# Revit family: Hager-UNIVERS-Surface_mounted-IP44-With_Cover-With_DIN-Hosted-DE-de
name_source: partatom
category: Electrical Equipment
units: mm (PartAtom-declared; Revit-internal decimal feet)

## family parameters
Cut with Voids When Loaded = No
Host = Face
Maintain Annotation Orientation = Yes
Panel Configuration = Two Columns, Circuits Across
Part Type = Panelboard
Room Calculation Point = No
Round Connector Dimension = Use Diameter
Shared = No

## types (114) — shared parameters
BC_MODEL_ID = 1539184
BC_OBJECT_ID = 512283
BC_OBJECT_VERSION = #6
Code hager = ADD-EC000214_EU
EF000007 - Farbe = weiß
EF000024 - UV-beständig = No
EF000049 - Tiefe = 165 mm  [stored 0.541339 ft]
EF000116 - RAL-Nummer = 9010
EF000118 - Mit Montageplatte = No
EF001062 - EMV-Ausführung = No
EF001088 - Anbaumöglichkeit = Yes
EF001134 - DIN-Schiene = Yes
EF004462 - Art der Schließung = sonstige
EF005474 - Schutzart (IP) = IP44
EF006306 - Mit Schloss = No
EF015941 - Signaldurchlassende Tür = No
ETIM class code = EC000214
ETIM class name = Small distribution board
HG000002-Mit tür = Yes
HG000003-Bereich = UNIVERS
HG000005-Dicke = 2 mm  [stored 0.00656168 ft]
HG000006-Flush mounted = No
HG000011-Leere Reihen von unten = No
HG000012-Türschwenkwinkel = 90.00°
HG000013-Tür links = No
HG000014-Tür rechts = Yes
HG000015-Sichtbarkeit der Türöffnung = Yes
HG000016-3D-Türsichtbarkeit = Yes
HG000017-Distanz zwischen den Polen = 18 mm  [stored 0.0590551 ft]
HG000060-RAL-number = 9010
HG000099-Onfly Template ID-de-DE = 507532
Manufacturer = Hager
Name = Hager-UNIVERS-Surface_mounted-IP44-With_Cover-With_DIN-NoHosted-DE-de
Name BIM&CO = Electricity
Name hager = ADD_Enclosures_EC000214
Uniformat = Low Tension Service & Dist.
Uniformat code = D501001
zero-valued in all types: Default Elevation, EF001131 - Innentiefe

## per-type parameters (varying)
| type | BC_VARIANT_ID | EF000003 - Montageart | EF000008 - Breite | EF000040 - Höhe | EF000218 - Einbautiefe | EF000266 - Anzahl der Reihen | EF000332 - Einbauhöhe | EF000846 - Einbaubreite | EF002950 - Breite in Teilungseinheiten | EF006244 - Transparenter Deckel/Tür | EF009212 - Ausführung Deckel | EF015776 - Erdungsklemmenblock | EF015777 - Neutralleiterklemmenblock | HG000001-Anzahl der Spalten | HG000004-Herstellerreferenz | HG000007-Anzahl der leeren Spalten | HG000008-Anzahl der leeren Reihen | HG000009-Doppelflügeligen Tür | HG000010-Asymmetrische Türen | HGEF000266-Anzahl der Reihen | HGEF0002950-Breite in Teilungseinheiten |
| UNIVERS-Surface_mounted_W300_H500_D165_12_Modular_Spacing-FWB31 | 1169536 | Aufputz | 300 mm | 500 mm  [stored 1.64042 ft] | 161 mm  [stored 0.528215 ft] | 3 | 500 mm  [stored 1.64042 ft] | 300 mm | 12 | No | mit Ausschnitt | No | Yes | 1 | FWB31 | 0 | 0 | No | No | 3 | 12 |
| UNIVERS-Surface_mounted_W300_H500_D165_12_Modular_Spacing-FWB31A | 1169538 | Aufputz | 300 mm | 500 mm  [stored 1.64042 ft] | 161 mm  [stored 0.528215 ft] | 3 | 500 mm  [stored 1.64042 ft] | 300 mm | 12 | No | mit Ausschnitt | No | No | 1 | FWB31A | 0 | 0 | No | No | 3 | 12 |
| UNIVERS-Surface_mounted_W300_H500_D165_12_Modular_Spacing-FWB31GS | 1169539 | Aufputz | 300 mm | 500 mm  [stored 1.64042 ft] | 161 mm  [stored 0.528215 ft] | 3 | 500 mm  [stored 1.64042 ft] | 300 mm | 12 | Yes | mit Ausschnitt | Yes | Yes | 1 | FWB31GS | 0 | 0 | No | No | 3 | 12 |
| UNIVERS-Surface_mounted_W300_H500_D165_12_Modular_Spacing-FWB31P | 1169540 | Aufputz | 300 mm | 500 mm  [stored 1.64042 ft] | 161 mm  [stored 0.528215 ft] | 3 | 500 mm  [stored 1.64042 ft] | 300 mm | 12 | No | geschlossen | No | No | 1 | FWB31P | 0 | 0 | No | No | 3 | 12 |
| UNIVERS-Surface_mounted_W300_H500_D165_12_Modular_Spacing-FWB31S | 1169541 | Aufputz | 300 mm | 500 mm  [stored 1.64042 ft] | 161 mm  [stored 0.528215 ft] | 3 | 500 mm  [stored 1.64042 ft] | 300 mm | 12 | No | mit Ausschnitt | Yes | Yes | 1 | FWB31S | 0 | 0 | No | No | 3 | 12 |
| UNIVERS-Surface_mounted_W550_H500_D165_24_Modular_Spacing-FWB32 | 1169543 | Aufputz | 550 mm | 500 mm  [stored 1.64042 ft] | 161 mm  [stored 0.528215 ft] | 3 | 500 mm  [stored 1.64042 ft] | 550 mm | 24 | No | mit Ausschnitt | No | Yes | 2 | FWB32 | 0 | 0 | No | No | 3 | 24 |
| UNIVERS-Surface_mounted_W550_H500_D165_24_Modular_Spacing-FWB32A | 1169545 | Aufputz | 550 mm | 500 mm  [stored 1.64042 ft] | 161 mm  [stored 0.528215 ft] | 3 | 500 mm  [stored 1.64042 ft] | 550 mm | 24 | No | mit Ausschnitt | No | No | 2 | FWB32A | 0 | 0 | No | No | 3 | 24 |
| UNIVERS-Surface_mounted_W550_H500_D165_24_Modular_Spacing-FWB32GS | 1169546 | Aufputz | 550 mm | 500 mm  [stored 1.64042 ft] | 161 mm  [stored 0.528215 ft] | 3 | 500 mm  [stored 1.64042 ft] | 550 mm | 24 | Yes | mit Ausschnitt | Yes | Yes | 2 | FWB32GS | 0 | 0 | No | No | 3 | 24 |
| UNIVERS-Surface_mounted_W550_H500_D165_24_Modular_Spacing-FWB32P | 1169547 | Aufputz | 550 mm | 500 mm  [stored 1.64042 ft] | 161 mm  [stored 0.528215 ft] | 3 | 500 mm  [stored 1.64042 ft] | 550 mm | 24 | No | geschlossen | No | No | 2 | FWB32P | 0 | 0 | No | No | 3 | 24 |
| UNIVERS-Surface_mounted_W550_H500_D165_24_Modular_Spacing-FWB32S | 1169549 | Aufputz | 550 mm | 500 mm  [stored 1.64042 ft] | 161 mm  [stored 0.528215 ft] | 3 | 500 mm  [stored 1.64042 ft] | 550 mm | 24 | No | mit Ausschnitt | Yes | Yes | 2 | FWB32S | 0 | 0 | No | No | 3 | 24 |
| UNIVERS-Surface_mounted_W800_H500_D165_36_Modular_Spacing-FWB33 | 1169551 | Aufputz | 800 mm  [stored 2.62467 ft] | 500 mm  [stored 1.64042 ft] | 161 mm  [stored 0.528215 ft] | 3 | 500 mm  [stored 1.64042 ft] | 800 mm  [stored 2.62467 ft] | 36 | No | mit Ausschnitt | No | Yes | 3 | FWB33 | 0 | 0 | Yes | Yes | 3 | 36 |
| UNIVERS-Surface_mounted_W800_H500_D165_36_Modular_Spacing-FWB33A | 1169553 | Aufputz | 800 mm  [stored 2.62467 ft] | 500 mm  [stored 1.64042 ft] | 161 mm  [stored 0.528215 ft] | 3 | 500 mm  [stored 1.64042 ft] | 800 mm  [stored 2.62467 ft] | 36 | No | mit Ausschnitt | No | No | 3 | FWB33A | 0 | 0 | Yes | Yes | 3 | 36 |
| UNIVERS-Surface_mounted_W800_H500_D165_36_Modular_Spacing-FWB33GS | 1169554 | Aufputz | 800 mm  [stored 2.62467 ft] | 500 mm  [stored 1.64042 ft] | 161 mm  [stored 0.528215 ft] | 3 | 500 mm  [stored 1.64042 ft] | 800 mm  [stored 2.62467 ft] | 36 | Yes | mit Ausschnitt | Yes | Yes | 3 | FWB33GS | 0 | 0 | Yes | Yes | 3 | 36 |
| UNIVERS-Surface_mounted_W800_H500_D165_36_Modular_Spacing-FWB33P | 1169556 | Aufputz | 800 mm  [stored 2.62467 ft] | 500 mm  [stored 1.64042 ft] | 161 mm  [stored 0.528215 ft] | 3 | 500 mm  [stored 1.64042 ft] | 800 mm  [stored 2.62467 ft] | 36 | No | mit Ausschnitt | No | No | 3 | FWB33P | 0 | 0 | Yes | Yes | 3 | 36 |
| UNIVERS-Surface_mounted_W800_H500_D165_36_Modular_Spacing-FWB33S | 1169558 | Aufputz | 800 mm  [stored 2.62467 ft] | 500 mm  [stored 1.64042 ft] | 161 mm  [stored 0.528215 ft] | 3 | 500 mm  [stored 1.64042 ft] | 800 mm  [stored 2.62467 ft] | 36 | No | mit Ausschnitt | Yes | Yes | 3 | FWB33S | 0 | 0 | Yes | Yes | 3 | 36 |
| UNIVERS-Surface_mounted_W1050_H500_D165_48_Modular_Spacing-FWB34 | 1169560 | Aufputz | 1050 mm | 500 mm  [stored 1.64042 ft] | 161 mm  [stored 0.528215 ft] | 3 | 500 mm  [stored 1.64042 ft] | 1050 mm | 48 | No | mit Ausschnitt | No | Yes | 4 | FWB34 | 0 | 0 | Yes | No | 3 | 48 |
| UNIVERS-Surface_mounted_W1050_H500_D165_48_Modular_Spacing-FWB34A | 1169562 | Aufputz | 1050 mm | 500 mm  [stored 1.64042 ft] | 161 mm  [stored 0.528215 ft] | 3 | 500 mm  [stored 1.64042 ft] | 1050 mm | 48 | No | mit Ausschnitt | No | No | 4 | FWB34A | 0 | 0 | Yes | No | 3 | 48 |
| UNIVERS-Surface_mounted_W1050_H500_D165_48_Modular_Spacing-FWB34GS | 1169564 | Aufputz | 1050 mm | 500 mm  [stored 1.64042 ft] | 161 mm  [stored 0.528215 ft] | 3 | 500 mm  [stored 1.64042 ft] | 1050 mm | 48 | Yes | mit Ausschnitt | Yes | Yes | 4 | FWB34GS | 0 | 0 | Yes | No | 3 | 48 |
| UNIVERS-Surface_mounted_W1050_H500_D165_48_Modular_Spacing-FWB34P | 1169567 | Aufputz | 1050 mm | 500 mm  [stored 1.64042 ft] | 161 mm  [stored 0.528215 ft] | 3 | 500 mm  [stored 1.64042 ft] | 1050 mm | 48 | No | geschlossen | No | No | 4 | FWB34P | 0 | 0 | Yes | No | 3 | 48 |
| UNIVERS-Surface_mounted_W1050_H500_D165_48_Modular_Spacing-FWB34S | 1169569 | Aufputz | 1050 mm | 500 mm  [stored 1.64042 ft] | 161 mm  [stored 0.528215 ft] | 3 | 500 mm  [stored 1.64042 ft] | 1050 mm | 48 | No | mit Ausschnitt | Yes | Yes | 4 | FWB34S | 0 | 0 | Yes | No | 3 | 48 |
| UNIVERS-Surface_mounted_W300_H650_D165_12_Modular_Spacing-FWB41 | 1169571 | Aufputz | 300 mm | 650 mm  [stored 2.13255 ft] | 161 mm  [stored 0.528215 ft] | 4 | 650 mm  [stored 2.13255 ft] | 300 mm | 12 | No | mit Ausschnitt | No | Yes | 1 | FWB41 | 0 | 0 | No | No | 4 | 12 |
| UNIVERS-Surface_mounted_W300_H650_D165_12_Modular_Spacing-FWB41A | 1169573 | Aufputz | 300 mm | 650 mm  [stored 2.13255 ft] | 161 mm  [stored 0.528215 ft] | 4 | 650 mm  [stored 2.13255 ft] | 300 mm | 12 | No | mit Ausschnitt | No | No | 1 | FWB41A | 0 | 0 | No | No | 4 | 12 |
| UNIVERS-Surface_mounted_W300_H650_D165_12_Modular_Spacing-FWB41GS | 1169574 | Aufputz | 300 mm | 650 mm  [stored 2.13255 ft] | 161 mm  [stored 0.528215 ft] | 4 | 650 mm  [stored 2.13255 ft] | 300 mm | 12 | Yes | mit Ausschnitt | Yes | Yes | 1 | FWB41GS | 0 | 0 | No | No | 4 | 12 |
| UNIVERS-Surface_mounted_W300_H650_D165_12_Modular_Spacing-FWB41P | 1169577 | Aufputz | 300 mm | 650 mm  [stored 2.13255 ft] | 161 mm  [stored 0.528215 ft] | 4 | 650 mm  [stored 2.13255 ft] | 300 mm | 12 | No | geschlossen | No | No | 1 | FWB41P | 0 | 0 | No | No | 4 | 12 |
| UNIVERS-Surface_mounted_W300_H650_D165_12_Modular_Spacing-FWB41S | 1169579 | Aufputz | 300 mm | 650 mm  [stored 2.13255 ft] | 161 mm  [stored 0.528215 ft] | 4 | 650 mm  [stored 2.13255 ft] | 300 mm | 12 | No | mit Ausschnitt | Yes | Yes | 1 | FWB41S | 0 | 0 | No | No | 4 | 12 |
| UNIVERS-Surface_mounted_W550_H650_D165_24_Modular_Spacing-FWB42 | 1169580 | Aufputz | 550 mm | 650 mm  [stored 2.13255 ft] | 161 mm  [stored 0.528215 ft] | 4 | 650 mm  [stored 2.13255 ft] | 550 mm | 24 | No | mit Ausschnitt | No | Yes | 2 | FWB42 | 0 | 0 | No | No | 4 | 24 |
| UNIVERS-Surface_mounted_W550_H650_D165_24_Modular_Spacing-FWB42A | 1169582 | Aufputz | 550 mm | 650 mm  [stored 2.13255 ft] | 161 mm  [stored 0.528215 ft] | 4 | 650 mm  [stored 2.13255 ft] | 550 mm | 24 | No | mit Ausschnitt | No | No | 2 | FWB42A | 0 | 0 | No | No | 4 | 24 |
| UNIVERS-Surface_mounted_W550_H650_D165_24_Modular_Spacing-FWB42GS | 1169584 | Aufputz | 550 mm | 650 mm  [stored 2.13255 ft] | 161 mm  [stored 0.528215 ft] | 4 | 650 mm  [stored 2.13255 ft] | 550 mm | 24 | Yes | mit Ausschnitt | Yes | Yes | 2 | FWB42GS | 0 | 0 | No | No | 4 | 24 |
| UNIVERS-Surface_mounted_W550_H650_D165_24_Modular_Spacing-FWB42P | 1169587 | Aufputz | 550 mm | 650 mm  [stored 2.13255 ft] | 161 mm  [stored 0.528215 ft] | 4 | 650 mm  [stored 2.13255 ft] | 550 mm | 24 | No | geschlossen | No | No | 2 | FWB42P | 0 | 0 | No | No | 4 | 24 |
| UNIVERS-Surface_mounted_W550_H650_D165_24_Modular_Spacing-FWB42P2 | 1169589 | Aufputz/Unterputz | 550 mm | 650 mm  [stored 2.13255 ft] | 161 mm  [stored 0.528215 ft] | 4 | 650 mm  [stored 2.13255 ft] | 550 mm | 24 | No | mit Ausschnitt | Yes | No | 1 | FWB42P2 | 1 | 0 | No | No | 4 | 24 |
| UNIVERS-Surface_mounted_W550_H650_D165_24_Modular_Spacing-FWB42S | 1169590 | Aufputz/Unterputz | 550 mm | 650 mm  [stored 2.13255 ft] | 161 mm  [stored 0.528215 ft] | 4 | 650 mm  [stored 2.13255 ft] | 550 mm | 24 | No | mit Ausschnitt | Yes | Yes | 2 | FWB42S | 0 | 0 | No | No | 4 | 24 |
| UNIVERS-Surface_mounted_W800_H650_D165_36_Modular_Spacing-FWB43 | 1169592 | Aufputz | 800 mm  [stored 2.62467 ft] | 650 mm  [stored 2.13255 ft] | 161 mm  [stored 0.528215 ft] | 4 | 650 mm  [stored 2.13255 ft] | 800 mm  [stored 2.62467 ft] | 36 | No | mit Ausschnitt | No | Yes | 3 | FWB43 | 0 | 0 | Yes | Yes | 4 | 36 |
| UNIVERS-Surface_mounted_W800_H650_D165_36_Modular_Spacing-FWB43A | 1169593 | Aufputz | 800 mm  [stored 2.62467 ft] | 650 mm  [stored 2.13255 ft] | 161 mm  [stored 0.528215 ft] | 4 | 650 mm  [stored 2.13255 ft] | 800 mm  [stored 2.62467 ft] | 36 | No | mit Ausschnitt | No | No | 3 | FWB43A | 0 | 0 | Yes | Yes | 4 | 36 |
| UNIVERS-Surface_mounted_W800_H650_D165_36_Modular_Spacing-FWB43GS | 1169596 | Aufputz | 800 mm  [stored 2.62467 ft] | 650 mm  [stored 2.13255 ft] | 161 mm  [stored 0.528215 ft] | 4 | 650 mm  [stored 2.13255 ft] | 800 mm  [stored 2.62467 ft] | 36 | Yes | mit Ausschnitt | Yes | Yes | 3 | FWB43GS | 0 | 0 | Yes | Yes | 4 | 36 |
| UNIVERS-Surface_mounted_W800_H650_D165_36_Modular_Spacing-FWB43P | 1169597 | Aufputz | 800 mm  [stored 2.62467 ft] | 650 mm  [stored 2.13255 ft] | 161 mm  [stored 0.528215 ft] | 4 | 650 mm  [stored 2.13255 ft] | 800 mm  [stored 2.62467 ft] | 36 | No | geschlossen | No | No | 3 | FWB43P | 0 | 0 | Yes | Yes | 4 | 36 |
| UNIVERS-Surface_mounted_W800_H650_D165_36_Modular_Spacing-FWB43S | 1169598 | Aufputz | 800 mm  [stored 2.62467 ft] | 650 mm  [stored 2.13255 ft] | 161 mm  [stored 0.528215 ft] | 4 | 650 mm  [stored 2.13255 ft] | 800 mm  [stored 2.62467 ft] | 36 | No | mit Ausschnitt | Yes | Yes | 3 | FWB43S | 0 | 0 | Yes | Yes | 4 | 36 |
| UNIVERS-Surface_mounted_W1050_H650_D165_48_Modular_Spacing-FWB44 | 1169599 | Aufputz | 1050 mm | 650 mm  [stored 2.13255 ft] | 161 mm  [stored 0.528215 ft] | 4 | 650 mm  [stored 2.13255 ft] | 1050 mm | 48 | No | mit Ausschnitt | No | Yes | 4 | FWB44 | 0 | 0 | Yes | No | 4 | 48 |
| UNIVERS-Surface_mounted_W1050_H650_D165_48_Modular_Spacing-FWB44A | 1169600 | Aufputz | 1050 mm | 650 mm  [stored 2.13255 ft] | 161 mm  [stored 0.528215 ft] | 4 | 650 mm  [stored 2.13255 ft] | 1050 mm | 48 | No | mit Ausschnitt | No | No | 4 | FWB44A | 0 | 0 | Yes | No | 4 | 48 |
| UNIVERS-Surface_mounted_W1050_H650_D165_48_Modular_Spacing-FWB44GS | 1169602 | Aufputz | 1050 mm | 650 mm  [stored 2.13255 ft] | 161 mm  [stored 0.528215 ft] | 4 | 650 mm  [stored 2.13255 ft] | 1050 mm | 48 | Yes | mit Ausschnitt | Yes | Yes | 4 | FWB44GS | 0 | 0 | Yes | No | 4 | 48 |
| UNIVERS-Surface_mounted_W1050_H650_D165_48_Modular_Spacing-FWB44P | 1169603 | Aufputz | 1050 mm | 650 mm  [stored 2.13255 ft] | 161 mm  [stored 0.528215 ft] | 4 | 650 mm  [stored 2.13255 ft] | 1050 mm | 48 | No | geschlossen | No | No | 4 | FWB44P | 0 | 0 | Yes | No | 4 | 48 |
| UNIVERS-Surface_mounted_W1050_H650_D165_48_Modular_Spacing-FWB44S | 1169604 | Aufputz | 1050 mm | 650 mm  [stored 2.13255 ft] | 161 mm  [stored 0.528215 ft] | 4 | 650 mm  [stored 2.13255 ft] | 1050 mm | 48 | No | mit Ausschnitt | Yes | Yes | 4 | FWB44S | 0 | 0 | Yes | No | 4 | 48 |
| UNIVERS-Surface_mounted_W300_H800_D165_12_Modular_Spacing-FWB51 | 1169606 | Aufputz | 300 mm | 800 mm  [stored 2.62467 ft] | 161 mm  [stored 0.528215 ft] | 5 | 800 mm  [stored 2.62467 ft] | 300 mm | 12 | No | mit Ausschnitt | No | Yes | 1 | FWB51 | 0 | 0 | No | No | 5 | 12 |
| UNIVERS-Surface_mounted_W300_H800_D165_12_Modular_Spacing-FWB51A | 1169608 | Aufputz | 300 mm | 800 mm  [stored 2.62467 ft] | 161 mm  [stored 0.528215 ft] | 5 | 800 mm  [stored 2.62467 ft] | 300 mm | 12 | No | mit Ausschnitt | No | No | 1 | FWB51A | 0 | 0 | No | No | 5 | 12 |
| UNIVERS-Surface_mounted_W300_H800_D165_12_Modular_Spacing-FWB51GS | 1169609 | Aufputz | 300 mm | 800 mm  [stored 2.62467 ft] | 161 mm  [stored 0.528215 ft] | 5 | 800 mm  [stored 2.62467 ft] | 300 mm | 12 | Yes | mit Ausschnitt | Yes | Yes | 1 | FWB51GS | 0 | 0 | No | No | 5 | 12 |
| UNIVERS-Surface_mounted_W300_H800_D165_12_Modular_Spacing-FWB51P | 1169610 | Aufputz | 300 mm | 800 mm  [stored 2.62467 ft] | 161 mm  [stored 0.528215 ft] | 5 | 800 mm  [stored 2.62467 ft] | 300 mm | 12 | No | geschlossen | No | No | 1 | FWB51P | 0 | 0 | No | No | 5 | 12 |
| UNIVERS-Surface_mounted_W300_H800_D165_12_Modular_Spacing-FWB51S | 1169612 | Aufputz | 300 mm | 800 mm  [stored 2.62467 ft] | 161 mm  [stored 0.528215 ft] | 5 | 800 mm  [stored 2.62467 ft] | 300 mm | 12 | No | mit Ausschnitt | Yes | Yes | 1 | FWB51S | 0 | 0 | No | No | 5 | 12 |
| UNIVERS-Surface_mounted_W550_H800_D165_24_Modular_Spacing-FWB52 | 1169613 | Aufputz | 550 mm | 800 mm  [stored 2.62467 ft] | 161 mm  [stored 0.528215 ft] | 5 | 800 mm  [stored 2.62467 ft] | 550 mm | 24 | No | mit Ausschnitt | No | Yes | 2 | FWB52 | 0 | 0 | No | No | 5 | 24 |
| UNIVERS-Surface_mounted_W550_H800_D165_24_Modular_Spacing-FWB52A | 1169614 | Aufputz | 550 mm | 800 mm  [stored 2.62467 ft] | 161 mm  [stored 0.528215 ft] | 5 | 800 mm  [stored 2.62467 ft] | 550 mm | 24 | No | mit Ausschnitt | No | No | 2 | FWB52A | 0 | 0 | No | No | 5 | 24 |
| UNIVERS-Surface_mounted_W550_H800_D165_24_Modular_Spacing-FWB52GS | 1169616 | Aufputz | 550 mm | 800 mm  [stored 2.62467 ft] | 161 mm  [stored 0.528215 ft] | 5 | 800 mm  [stored 2.62467 ft] | 550 mm | 24 | Yes | mit Ausschnitt | Yes | Yes | 2 | FWB52GS | 0 | 0 | No | No | 5 | 24 |
| UNIVERS-Surface_mounted_W550_H800_D165_24_Modular_Spacing-FWB52N | 1169617 | Aufputz | 550 mm | 800 mm  [stored 2.62467 ft] | 161 mm  [stored 0.528215 ft] | 5 | 800 mm  [stored 2.62467 ft] | 550 mm | 24 | No | mit Ausschnitt | No | No | 2 | FWB52N | 0 | 2 | No | No | 5 | 24 |
| UNIVERS-Surface_mounted_W550_H800_D165_24_Modular_Spacing-FWB52N3 | 1169618 | Aufputz | 550 mm | 800 mm  [stored 2.62467 ft] | 160 mm  [stored 0.524934 ft] | 5 | 800 mm  [stored 2.62467 ft] | 550 mm | 24 | No | mit Ausschnitt | No | No | 2 | FWB52N3 | 0 | 2 | No | No | 5 | 24 |
| UNIVERS-Surface_mounted_W550_H800_D165_24_Modular_Spacing-FWB52P | 1169619 | Aufputz | 550 mm | 800 mm  [stored 2.62467 ft] | 161 mm  [stored 0.528215 ft] | 5 | 800 mm  [stored 2.62467 ft] | 550 mm | 24 | No | geschlossen | No | No | 2 | FWB52P | 0 | 0 | No | No | 5 | 24 |
| UNIVERS-Surface_mounted_W550_H800_D165_24_Modular_Spacing-FWB52P2 | 1169621 | Aufputz/Unterputz | 550 mm | 800 mm  [stored 2.62467 ft] | 161 mm  [stored 0.528215 ft] | 5 | 800 mm  [stored 2.62467 ft] | 550 mm | 24 | No | mit Ausschnitt | Yes | No | 1 | FWB52P2 | 1 | 0 | No | No | 5 | 24 |
| UNIVERS-Surface_mounted_W550_H800_D165_24_Modular_Spacing-FWB52S | 1169622 | Aufputz | 550 mm | 800 mm  [stored 2.62467 ft] | 161 mm  [stored 0.528215 ft] | 5 | 800 mm  [stored 2.62467 ft] | 550 mm | 24 | No | mit Ausschnitt | Yes | Yes | 2 | FWB52S | 0 | 0 | No | No | 5 | 24 |
| UNIVERS-Surface_mounted_W800_H800_D165_36_Modular_Spacing-FWB53 | 1169624 | Aufputz | 800 mm  [stored 2.62467 ft] | 800 mm  [stored 2.62467 ft] | 161 mm  [stored 0.528215 ft] | 5 | 800 mm  [stored 2.62467 ft] | 800 mm  [stored 2.62467 ft] | 36 | No | mit Ausschnitt | No | Yes | 3 | FWB53 | 0 | 0 | Yes | Yes | 5 | 36 |
| UNIVERS-Surface_mounted_W800_H800_D165_36_Modular_Spacing-FWB53A | 1169625 | Aufputz | 800 mm  [stored 2.62467 ft] | 800 mm  [stored 2.62467 ft] | 161 mm  [stored 0.528215 ft] | 5 | 800 mm  [stored 2.62467 ft] | 800 mm  [stored 2.62467 ft] | 36 | No | mit Ausschnitt | No | No | 3 | FWB53A | 0 | 0 | Yes | Yes | 5 | 36 |
| UNIVERS-Surface_mounted_W800_H800_D165_36_Modular_Spacing-FWB53GS | 1169627 | Aufputz | 800 mm  [stored 2.62467 ft] | 800 mm  [stored 2.62467 ft] | 161 mm  [stored 0.528215 ft] | 5 | 800 mm  [stored 2.62467 ft] | 800 mm  [stored 2.62467 ft] | 36 | Yes | mit Ausschnitt | Yes | Yes | 3 | FWB53GS | 0 | 0 | Yes | Yes | 5 | 36 |
| UNIVERS-Surface_mounted_W800_H800_D165_36_Modular_Spacing-FWB53N | 1169628 | Aufputz | 800 mm  [stored 2.62467 ft] | 800 mm  [stored 2.62467 ft] | 161 mm  [stored 0.528215 ft] | 5 | 800 mm  [stored 2.62467 ft] | 800 mm  [stored 2.62467 ft] | 36 | No | mit Ausschnitt | No | No | 3 | FWB53N | 0 | 2 | Yes | Yes | 5 | 36 |
| UNIVERS-Surface_mounted_W800_H800_D165_36_Modular_Spacing-FWB53N3 | 1169629 | Aufputz | 800 mm  [stored 2.62467 ft] | 800 mm  [stored 2.62467 ft] | 161 mm  [stored 0.528215 ft] | 5 | 800 mm  [stored 2.62467 ft] | 800 mm  [stored 2.62467 ft] | 36 | No | mit Ausschnitt | No | No | 3 | FWB53N3 | 0 | 2 | Yes | Yes | 5 | 36 |
| UNIVERS-Surface_mounted_W800_H800_D165_36_Modular_Spacing-FWB53P | 1169631 | Aufputz | 800 mm  [stored 2.62467 ft] | 800 mm  [stored 2.62467 ft] | 161 mm  [stored 0.528215 ft] | 5 | 800 mm  [stored 2.62467 ft] | 800 mm  [stored 2.62467 ft] | 36 | No | geschlossen | No | No | 3 | FWB53P | 0 | 0 | Yes | No | 5 | 36 |
| UNIVERS-Surface_mounted_W800_H800_D165_36_Modular_Spacing-FWB53S | 1169633 | Aufputz | 800 mm  [stored 2.62467 ft] | 800 mm  [stored 2.62467 ft] | 161 mm  [stored 0.528215 ft] | 5 | 800 mm  [stored 2.62467 ft] | 800 mm  [stored 2.62467 ft] | 36 | No | mit Ausschnitt | Yes | Yes | 3 | FWB53S | 0 | 0 | Yes | Yes | 5 | 36 |
| UNIVERS-Surface_mounted_W1050_H800_D165_48_Modular_Spacing-FWB54 | 1169634 | Aufputz | 1050 mm | 800 mm  [stored 2.62467 ft] | 161 mm  [stored 0.528215 ft] | 5 | 800 mm  [stored 2.62467 ft] | 1050 mm | 48 | No | mit Ausschnitt | No | Yes | 4 | FWB54 | 0 | 0 | Yes | No | 5 | 48 |
| UNIVERS-Surface_mounted_W1050_H800_D165_48_Modular_Spacing-FWB54A | 1169635 | Aufputz | 1050 mm | 800 mm  [stored 2.62467 ft] | 161 mm  [stored 0.528215 ft] | 5 | 800 mm  [stored 2.62467 ft] | 1050 mm | 48 | No | mit Ausschnitt | No | No | 4 | FWB54A | 0 | 0 | Yes | No | 5 | 48 |
| UNIVERS-Surface_mounted_W1050_H800_D165_48_Modular_Spacing-FWB54GS | 1169636 | Aufputz | 1050 mm | 800 mm  [stored 2.62467 ft] | 161 mm  [stored 0.528215 ft] | 5 | 800 mm  [stored 2.62467 ft] | 1050 mm | 48 | Yes | mit Ausschnitt | Yes | Yes | 4 | FWB54GS | 0 | 0 | Yes | No | 5 | 48 |
| UNIVERS-Surface_mounted_W1050_H800_D165_48_Modular_Spacing-FWB54P | 1169638 | Aufputz | 1050 mm | 800 mm  [stored 2.62467 ft] | 161 mm  [stored 0.528215 ft] | 5 | 800 mm  [stored 2.62467 ft] | 1050 mm | 48 | No | geschlossen | No | No | 4 | FWB54P | 0 | 0 | Yes | No | 5 | 48 |
| UNIVERS-Surface_mounted_W1050_H800_D165_48_Modular_Spacing-FWB54S | 1169640 | Aufputz | 1050 mm | 800 mm  [stored 2.62467 ft] | 161 mm  [stored 0.528215 ft] | 5 | 800 mm  [stored 2.62467 ft] | 1050 mm | 48 | No | mit Ausschnitt | Yes | Yes | 4 | FWB54S | 0 | 0 | Yes | No | 5 | 48 |
| UNIVERS-Surface_mounted_W300_H950_D165_12_Modular_Spacing-FWB61 | 1169641 | Aufputz | 300 mm | 950 mm  [stored 3.1168 ft] | 161 mm  [stored 0.528215 ft] | 6 | 950 mm  [stored 3.1168 ft] | 300 mm | 12 | No | mit Ausschnitt | No | Yes | 1 | FWB61 | 0 | 0 | No | No | 6 | 12 |
| UNIVERS-Surface_mounted_W300_H950_D165_12_Modular_Spacing-FWB61A | 1169642 | Aufputz | 300 mm | 950 mm  [stored 3.1168 ft] | 161 mm  [stored 0.528215 ft] | 6 | 950 mm  [stored 3.1168 ft] | 300 mm | 12 | No | mit Ausschnitt | No | No | 1 | FWB61A | 0 | 0 | No | No | 6 | 12 |
| UNIVERS-Surface_mounted_W300_H950_D165_12_Modular_Spacing-FWB61GS | 1169644 | Aufputz | 300 mm | 950 mm  [stored 3.1168 ft] | 161 mm  [stored 0.528215 ft] | 6 | 950 mm  [stored 3.1168 ft] | 300 mm | 12 | Yes | mit Ausschnitt | Yes | Yes | 1 | FWB61GS | 0 | 0 | No | No | 6 | 12 |
| UNIVERS-Surface_mounted_W300_H950_D165_12_Modular_Spacing-FWB61P | 1169646 | Aufputz | 300 mm | 950 mm  [stored 3.1168 ft] | 161 mm  [stored 0.528215 ft] | 6 | 950 mm  [stored 3.1168 ft] | 300 mm | 12 | No | geschlossen | No | No | 1 | FWB61P | 0 | 0 | No | No | 6 | 12 |
| UNIVERS-Surface_mounted_W300_H950_D165_12_Modular_Spacing-FWB61S | 1169647 | Aufputz | 300 mm | 950 mm  [stored 3.1168 ft] | 161 mm  [stored 0.528215 ft] | 6 | 950 mm  [stored 3.1168 ft] | 300 mm | 12 | No | mit Ausschnitt | Yes | Yes | 1 | FWB61S | 0 | 0 | No | No | 6 | 12 |
| UNIVERS-Surface_mounted_W550_H950_D165_24_Modular_Spacing-FWB62 | 1169648 | Aufputz | 550 mm | 950 mm  [stored 3.1168 ft] | 161 mm  [stored 0.528215 ft] | 6 | 950 mm  [stored 3.1168 ft] | 550 mm | 24 | No | mit Ausschnitt | No | Yes | 2 | FWB62 | 0 | 0 | No | No | 6 | 24 |
| UNIVERS-Surface_mounted_W550_H950_D165_24_Modular_Spacing-FWB62A | 1169649 | Aufputz | 550 mm | 950 mm  [stored 3.1168 ft] | 161 mm  [stored 0.528215 ft] | 6 | 950 mm  [stored 3.1168 ft] | 550 mm | 24 | No | mit Ausschnitt | No | No | 2 | FWB62A | 0 | 0 | No | No | 6 | 24 |
| UNIVERS-Surface_mounted_W550_H950_D165_24_Modular_Spacing-FWB62GS | 1169652 | Aufputz | 550 mm | 950 mm  [stored 3.1168 ft] | 161 mm  [stored 0.528215 ft] | 6 | 950 mm  [stored 3.1168 ft] | 550 mm | 24 | Yes | mit Ausschnitt | Yes | Yes | 2 | FWB62GS | 0 | 0 | No | No | 6 | 24 |
| UNIVERS-Surface_mounted_W550_H950_D165_24_Modular_Spacing-FWB62N | 1169653 | Aufputz | 550 mm | 950 mm  [stored 3.1168 ft] | 161 mm  [stored 0.528215 ft] | 6 | 950 mm  [stored 3.1168 ft] | 550 mm | 24 | No | mit Ausschnitt | No | No | 2 | FWB62N | 0 | 2 | No | No | 6 | 24 |
| UNIVERS-Surface_mounted_W550_H950_D165_24_Modular_Spacing-FWB62N3 | 1169654 | Aufputz | 550 mm | 950 mm  [stored 3.1168 ft] | 161 mm  [stored 0.528215 ft] | 6 | 950 mm  [stored 3.1168 ft] | 550 mm | 24 | No | mit Ausschnitt | No | No | 2 | FWB62N3 | 0 | 2 | No | No | 6 | 24 |
| UNIVERS-Surface_mounted_W550_H950_D165_24_Modular_Spacing-FWB62P | 1169657 | Aufputz | 550 mm | 950 mm  [stored 3.1168 ft] | 161 mm  [stored 0.528215 ft] | 6 | 950 mm  [stored 3.1168 ft] | 550 mm | 24 | No | geschlossen | No | No | 2 | FWB62P | 0 | 0 | No | No | 6 | 24 |
| UNIVERS-Surface_mounted_W550_H950_D165_24_Modular_Spacing-FWB62S | 1169658 | Aufputz | 550 mm | 950 mm  [stored 3.1168 ft] | 161 mm  [stored 0.528215 ft] | 6 | 950 mm  [stored 3.1168 ft] | 550 mm | 24 | No | mit Ausschnitt | Yes | Yes | 2 | FWB62S | 0 | 0 | No | No | 6 | 24 |
| UNIVERS-Surface_mounted_W800_H950_D165_36_Modular_Spacing-FWB63 | 1169659 | Aufputz | 800 mm  [stored 2.62467 ft] | 950 mm  [stored 3.1168 ft] | 161 mm  [stored 0.528215 ft] | 6 | 950 mm  [stored 3.1168 ft] | 800 mm  [stored 2.62467 ft] | 36 | No | mit Ausschnitt | No | Yes | 3 | FWB63 | 0 | 0 | Yes | Yes | 6 | 36 |
| UNIVERS-Surface_mounted_W800_H950_D165_36_Modular_Spacing-FWB63A | 1169660 | Aufputz | 800 mm  [stored 2.62467 ft] | 950 mm  [stored 3.1168 ft] | 161 mm  [stored 0.528215 ft] | 6 | 950 mm  [stored 3.1168 ft] | 800 mm  [stored 2.62467 ft] | 36 | No | mit Ausschnitt | No | No | 3 | FWB63A | 0 | 0 | Yes | Yes | 6 | 36 |
| UNIVERS-Surface_mounted_W800_H950_D165_36_Modular_Spacing-FWB63GS | 1169663 | Aufputz | 800 mm  [stored 2.62467 ft] | 950 mm  [stored 3.1168 ft] | 161 mm  [stored 0.528215 ft] | 6 | 950 mm  [stored 3.1168 ft] | 800 mm  [stored 2.62467 ft] | 36 | Yes | mit Ausschnitt | Yes | Yes | 3 | FWB63GS | 0 | 0 | Yes | Yes | 6 | 36 |
| UNIVERS-Surface_mounted_W800_H950_D165_36_Modular_Spacing-FWB63N | 1169664 | Aufputz | 800 mm  [stored 2.62467 ft] | 950 mm  [stored 3.1168 ft] | 161 mm  [stored 0.528215 ft] | 6 | 950 mm  [stored 3.1168 ft] | 800 mm  [stored 2.62467 ft] | 36 | No | mit Ausschnitt | No | No | 3 | FWB63N | 0 | 2 | Yes | Yes | 6 | 36 |
| UNIVERS-Surface_mounted_W800_H950_D165_36_Modular_Spacing-FWB63N3 | 1169665 | Aufputz | 800 mm  [stored 2.62467 ft] | 950 mm  [stored 3.1168 ft] | 161 mm  [stored 0.528215 ft] | 6 | 950 mm  [stored 3.1168 ft] | 800 mm  [stored 2.62467 ft] | 36 | No | mit Ausschnitt | No | No | 3 | FWB63N3 | 0 | 2 | Yes | Yes | 6 | 36 |
| UNIVERS-Surface_mounted_W800_H950_D165_36_Modular_Spacing-FWB63P | 1169666 | Aufputz | 800 mm  [stored 2.62467 ft] | 950 mm  [stored 3.1168 ft] | 161 mm  [stored 0.528215 ft] | 6 | 950 mm  [stored 3.1168 ft] | 800 mm  [stored 2.62467 ft] | 36 | No | geschlossen | No | No | 3 | FWB63P | 0 | 0 | Yes | No | 6 | 36 |
| UNIVERS-Surface_mounted_W800_H950_D165_36_Modular_Spacing-FWB63S | 1169667 | Aufputz | 800 mm  [stored 2.62467 ft] | 950 mm  [stored 3.1168 ft] | 161 mm  [stored 0.528215 ft] | 6 | 950 mm  [stored 3.1168 ft] | 800 mm  [stored 2.62467 ft] | 36 | No | mit Ausschnitt | Yes | Yes | 3 | FWB63S | 0 | 0 | Yes | Yes | 6 | 36 |
| UNIVERS-Surface_mounted_W1050_H950_D165_48_Modular_Spacing-FWB64 | 1169669 | Aufputz | 1050 mm | 950 mm  [stored 3.1168 ft] | 161 mm  [stored 0.528215 ft] | 6 | 950 mm  [stored 3.1168 ft] | 1050 mm | 48 | No | mit Ausschnitt | No | Yes | 4 | FWB64 | 0 | 0 | Yes | No | 6 | 48 |
| UNIVERS-Surface_mounted_W1050_H950_D165_48_Modular_Spacing-FWB64A | 1169670 | Aufputz | 1050 mm | 950 mm  [stored 3.1168 ft] | 161 mm  [stored 0.528215 ft] | 6 | 950 mm  [stored 3.1168 ft] | 1050 mm | 48 | No | mit Ausschnitt | No | No | 4 | FWB64A | 0 | 0 | Yes | No | 6 | 48 |
| UNIVERS-Surface_mounted_W1050_H950_D165_48_Modular_Spacing-FWB64GS | 1169671 | Aufputz | 1050 mm | 950 mm  [stored 3.1168 ft] | 161 mm  [stored 0.528215 ft] | 6 | 950 mm  [stored 3.1168 ft] | 1050 mm | 48 | Yes | mit Ausschnitt | Yes | Yes | 4 | FWB64GS | 0 | 0 | Yes | No | 6 | 48 |
| UNIVERS-Surface_mounted_W1050_H950_D165_48_Modular_Spacing-FWB64N | 1169672 | Aufputz | 1050 mm | 950 mm  [stored 3.1168 ft] | 161 mm  [stored 0.528215 ft] | 6 | 950 mm  [stored 3.1168 ft] | 1050 mm | 48 | No | mit Ausschnitt | No | No | 4 | FWB64N | 0 | 2 | Yes | No | 6 | 48 |
| UNIVERS-Surface_mounted_W1050_H950_D165_48_Modular_Spacing-FWB64N3 | 1169674 | Aufputz | 1050 mm | 950 mm  [stored 3.1168 ft] | 161 mm  [stored 0.528215 ft] | 6 | 950 mm  [stored 3.1168 ft] | 1050 mm | 48 | No | mit Ausschnitt | No | No | 4 | FWB64N3 | 0 | 2 | Yes | No | 6 | 48 |
| UNIVERS-Surface_mounted_W1050_H950_D165_48_Modular_Spacing-FWB64P | 1169675 | Aufputz | 1050 mm | 950 mm  [stored 3.1168 ft] | 161 mm  [stored 0.528215 ft] | 6 | 950 mm  [stored 3.1168 ft] | 1050 mm | 48 | No | geschlossen | No | No | 4 | FWB64P | 0 | 0 | Yes | No | 6 | 48 |
| UNIVERS-Surface_mounted_W1050_H950_D165_48_Modular_Spacing-FWB64S | 1169676 | Aufputz | 1050 mm | 950 mm  [stored 3.1168 ft] | 161 mm  [stored 0.528215 ft] | 6 | 950 mm  [stored 3.1168 ft] | 1050 mm | 48 | No | mit Ausschnitt | Yes | Yes | 4 | FWB64S | 0 | 0 | Yes | No | 6 | 48 |
| UNIVERS-Surface_mounted_W300_H1100_D165_12_Modular_Spacing-FWB71 | 1169677 | Aufputz | 300 mm | 1100 mm  [stored 3.60892 ft] | 161 mm  [stored 0.528215 ft] | 7 | 1100 mm  [stored 3.60892 ft] | 300 mm | 12 | No | mit Ausschnitt | No | Yes | 1 | FWB71 | 0 | 0 | No | No | 7 | 12 |
| UNIVERS-Surface_mounted_W300_H1100_D165_12_Modular_Spacing-FWB71A | 1169679 | Aufputz | 300 mm | 1100 mm  [stored 3.60892 ft] | 161 mm  [stored 0.528215 ft] | 7 | 1100 mm  [stored 3.60892 ft] | 300 mm | 12 | No | mit Ausschnitt | No | No | 1 | FWB71A | 0 | 0 | No | No | 7 | 12 |
| UNIVERS-Surface_mounted_W300_H1100_D165_12_Modular_Spacing-FWB71GS | 1169680 | Aufputz | 300 mm | 1100 mm  [stored 3.60892 ft] | 161 mm  [stored 0.528215 ft] | 7 | 1100 mm  [stored 3.60892 ft] | 300 mm | 12 | Yes | mit Ausschnitt | Yes | Yes | 1 | FWB71GS | 0 | 0 | No | No | 7 | 12 |
| UNIVERS-Surface_mounted_W300_H1100_D165_12_Modular_Spacing-FWB71S | 1169681 | Aufputz | 300 mm | 1100 mm  [stored 3.60892 ft] | 161 mm  [stored 0.528215 ft] | 7 | 1100 mm  [stored 3.60892 ft] | 300 mm | 12 | No | mit Ausschnitt | Yes | Yes | 1 | FWB71S | 0 | 0 | No | No | 7 | 12 |
| UNIVERS-Surface_mounted_W550_H1100_D165_24_Modular_Spacing-FWB72 | 1169682 | Aufputz | 550 mm | 1100 mm  [stored 3.60892 ft] | 161 mm  [stored 0.528215 ft] | 7 | 1100 mm  [stored 3.60892 ft] | 550 mm | 24 | No | mit Ausschnitt | No | Yes | 2 | FWB72 | 0 | 0 | No | No | 7 | 24 |
| UNIVERS-Surface_mounted_W550_H1100_D165_24_Modular_Spacing-FWB72A | 1169684 | Aufputz | 550 mm | 1100 mm  [stored 3.60892 ft] | 161 mm  [stored 0.528215 ft] | 7 | 1100 mm  [stored 3.60892 ft] | 550 mm | 24 | No | mit Ausschnitt | No | No | 2 | FWB72A | 0 | 0 | No | No | 7 | 24 |
| UNIVERS-Surface_mounted_W550_H1100_D165_24_Modular_Spacing-FWB72GS | 1169685 | Aufputz | 550 mm | 1100 mm  [stored 3.60892 ft] | 161 mm  [stored 0.528215 ft] | 7 | 1100 mm  [stored 3.60892 ft] | 550 mm | 24 | Yes | mit Ausschnitt | Yes | Yes | 2 | FWB72GS | 0 | 0 | No | No | 7 | 24 |
| UNIVERS-Surface_mounted_W550_H1100_D165_24_Modular_Spacing-FWB72N | 1169686 | Aufputz | 550 mm | 1100 mm  [stored 3.60892 ft] | 161 mm  [stored 0.528215 ft] | 7 | 1100 mm  [stored 3.60892 ft] | 550 mm | 24 | No | mit Ausschnitt | No | No | 2 | FWB72N | 0 | 2 | No | No | 7 | 24 |
| UNIVERS-Surface_mounted_W550_H1100_D165_24_Modular_Spacing-FWB72N3 | 1169687 | Aufputz | 550 mm | 1100 mm  [stored 3.60892 ft] | 161 mm  [stored 0.528215 ft] | 7 | 1100 mm  [stored 3.60892 ft] | 550 mm | 24 | No | mit Ausschnitt | No | No | 2 | FWB72N3 | 0 | 2 | No | No | 7 | 24 |
| UNIVERS-Surface_mounted_W550_H1100_D165_24_Modular_Spacing-FWB72S | 1169689 | Aufputz/Unterputz | 550 mm | 1100 mm  [stored 3.60892 ft] | 161 mm  [stored 0.528215 ft] | 7 | 1100 mm  [stored 3.60892 ft] | 550 mm | 24 | No | mit Ausschnitt | Yes | Yes | 2 | FWB72S | 0 | 0 | No | No | 7 | 24 |
| UNIVERS-Surface_mounted_W800_H1100_D165_36_Modular_Spacing-FWB73 | 1169690 | Aufputz | 800 mm  [stored 2.62467 ft] | 1100 mm  [stored 3.60892 ft] | 161 mm  [stored 0.528215 ft] | 7 | 1100 mm  [stored 3.60892 ft] | 800 mm  [stored 2.62467 ft] | 36 | No | mit Ausschnitt | No | Yes | 3 | FWB73 | 0 | 0 | Yes | Yes | 7 | 36 |
| UNIVERS-Surface_mounted_W800_H1100_D165_36_Modular_Spacing-FWB73A | 1169691 | Aufputz | 800 mm  [stored 2.62467 ft] | 1100 mm  [stored 3.60892 ft] | 161 mm  [stored 0.528215 ft] | 7 | 1100 mm  [stored 3.60892 ft] | 800 mm  [stored 2.62467 ft] | 36 | No | mit Ausschnitt | No | No | 3 | FWB73A | 0 | 0 | Yes | Yes | 7 | 36 |
| UNIVERS-Surface_mounted_W800_H1100_D165_36_Modular_Spacing-FWB73GS | 1169692 | Aufputz | 800 mm  [stored 2.62467 ft] | 1100 mm  [stored 3.60892 ft] | 161 mm  [stored 0.528215 ft] | 7 | 1100 mm  [stored 3.60892 ft] | 800 mm  [stored 2.62467 ft] | 36 | Yes | mit Ausschnitt | Yes | Yes | 3 | FWB73GS | 0 | 0 | Yes | Yes | 7 | 36 |
| UNIVERS-Surface_mounted_W800_H1100_D165_36_Modular_Spacing-FWB73N | 1169694 | Aufputz | 800 mm  [stored 2.62467 ft] | 1100 mm  [stored 3.60892 ft] | 161 mm  [stored 0.528215 ft] | 7 | 1100 mm  [stored 3.60892 ft] | 800 mm  [stored 2.62467 ft] | 36 | No | mit Ausschnitt | No | No | 3 | FWB73N | 0 | 2 | Yes | Yes | 7 | 36 |
| UNIVERS-Surface_mounted_W800_H1100_D165_36_Modular_Spacing-FWB73N3 | 1169695 | Aufputz | 800 mm  [stored 2.62467 ft] | 1100 mm  [stored 3.60892 ft] | 161 mm  [stored 0.528215 ft] | 7 | 1100 mm  [stored 3.60892 ft] | 800 mm  [stored 2.62467 ft] | 36 | No | mit Ausschnitt | No | No | 3 | FWB73N3 | 0 | 2 | Yes | Yes | 7 | 36 |
| UNIVERS-Surface_mounted_W800_H1100_D165_36_Modular_Spacing-FWB73S | 1169696 | Aufputz/Unterputz | 800 mm  [stored 2.62467 ft] | 1100 mm  [stored 3.60892 ft] | 161 mm  [stored 0.528215 ft] | 7 | 1100 mm  [stored 3.60892 ft] | 800 mm  [stored 2.62467 ft] | 36 | No | mit Ausschnitt | Yes | Yes | 3 | FWB73S | 0 | 0 | Yes | Yes | 7 | 36 |
| UNIVERS-Surface_mounted_W1050_H1100_D165_48_Modular_Spacing-FWB74 | 1169697 | Aufputz | 1050 mm | 1100 mm  [stored 3.60892 ft] | 161 mm  [stored 0.528215 ft] | 7 | 1100 mm  [stored 3.60892 ft] | 1050 mm | 48 | No | mit Ausschnitt | No | Yes | 4 | FWB74 | 0 | 0 | Yes | No | 7 | 48 |
| UNIVERS-Surface_mounted_W1050_H1100_D165_48_Modular_Spacing-FWB74A | 1169699 | Aufputz | 1050 mm | 1100 mm  [stored 3.60892 ft] | 161 mm  [stored 0.528215 ft] | 7 | 1100 mm  [stored 3.60892 ft] | 1050 mm | 48 | No | mit Ausschnitt | No | No | 4 | FWB74A | 0 | 0 | Yes | No | 7 | 48 |
| UNIVERS-Surface_mounted_W1050_H1100_D165_48_Modular_Spacing-FWB74GS | 1169700 | Aufputz | 1050 mm | 1100 mm  [stored 3.60892 ft] | 161 mm  [stored 0.528215 ft] | 7 | 1100 mm  [stored 3.60892 ft] | 1050 mm | 48 | Yes | mit Ausschnitt | Yes | Yes | 4 | FWB74GS | 0 | 0 | Yes | No | 7 | 48 |
| UNIVERS-Surface_mounted_W1050_H1100_D165_48_Modular_Spacing-FWB74N | 1169701 | Aufputz | 1050 mm | 1100 mm  [stored 3.60892 ft] | 161 mm  [stored 0.528215 ft] | 7 | 1100 mm  [stored 3.60892 ft] | 1050 mm | 48 | No | mit Ausschnitt | No | No | 4 | FWB74N | 0 | 2 | Yes | No | 7 | 48 |
| UNIVERS-Surface_mounted_W1050_H1100_D165_48_Modular_Spacing-FWB74N3 | 1169702 | Aufputz | 1050 mm | 1100 mm  [stored 3.60892 ft] | 161 mm  [stored 0.528215 ft] | 7 | 1100 mm  [stored 3.60892 ft] | 1050 mm | 48 | No | mit Ausschnitt | No | No | 4 | FWB74N3 | 0 | 2 | Yes | No | 7 | 48 |
| UNIVERS-Surface_mounted_W1050_H1100_D165_48_Modular_Spacing-FWB74S | 1169703 | Aufputz/Unterputz | 1050 mm | 1100 mm  [stored 3.60892 ft] | 161 mm  [stored 0.528215 ft] | 7 | 1100 mm  [stored 3.60892 ft] | 1050 mm | 48 | No | mit Ausschnitt | Yes | Yes | 4 | FWB74S | 0 | 0 | Yes | No | 7 | 48 |

note: column(s) folded — value = type name in every type: Reference

note: [stored X ft] marks values corroborated as IEEE doubles in the binary element streams (Revit-internal decimal feet)

## geometry (parser evidence)
native form markers: Sweep x16
no freeform markers — native parametric forms only
